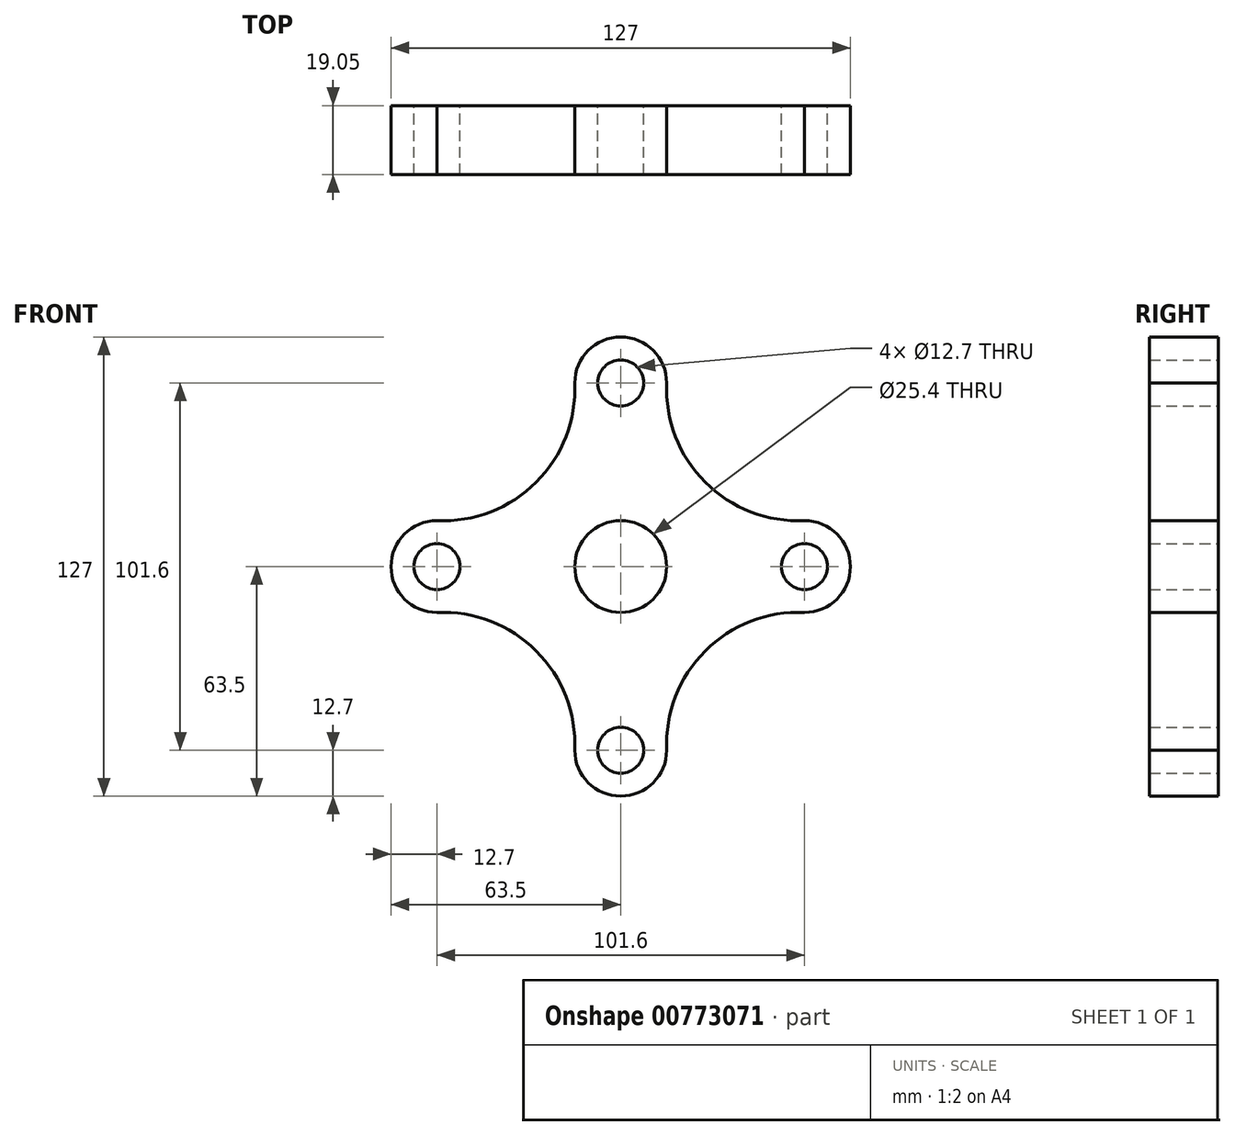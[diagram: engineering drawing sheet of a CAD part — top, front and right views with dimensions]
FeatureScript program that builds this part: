
annotation { "Feature Type Name" : "Feature", "Feature Type Description" : "" }
export const myFeature = defineFeature(function(context is Context, id is Id, definition is map)
    precondition{}
    {
        {
            var Q0;
            Q0=qCreatedBy(makeId("Front.planeOp"),FACE);
            var sketch = newSketch(context, id + "F0", { "sketchPlane" : qUnion([Q0])});
            skCircle(sketch, "E0", {"center": v(0, 50.8) * mm, "radius": 6.35 * mm});
            skArc(sketch, "E1", {"start": v(12.7, 50.8) * mm, "mid": v(0, 63.5) * mm, "end": v(-12.7, 50.8) * mm});
            skCircle(sketch, "E2.MirrorC", {"center": v(0, -50.8) * mm, "radius": 6.35 * mm});
            skArc(sketch, "E3.MirrorCS", {"start": v(12.7, -50.8) * mm, "mid": v(0, -63.5) * mm, "end": v(-12.7, -50.8) * mm});
            skCircle(sketch, "E4", {"center": v(-50.8, 0) * mm, "radius": 6.35 * mm});
            skArc(sketch, "E5", {"start": v(-50.8, 12.7) * mm, "mid": v(-63.5, 0) * mm, "end": v(-50.8, -12.7) * mm});
            skCircle(sketch, "E6.MirrorC", {"center": v(50.8, 0) * mm, "radius": 6.35 * mm});
            skArc(sketch, "E7.MirrorCS", {"start": v(50.8, 12.7) * mm, "mid": v(63.5, 0) * mm, "end": v(50.8, -12.7) * mm});
            skArc(sketch, "E8", {"start": v(-50.8, 12.7) * mm, "mid": v(-23.36, 23.36) * mm, "end": v(-12.7, 50.8) * mm});
            skArc(sketch, "E9", {"start": v(12.7, 50.8) * mm, "mid": v(23.36, 23.36) * mm, "end": v(50.8, 12.7) * mm});
            skArc(sketch, "E10", {"start": v(-12.7, -50.8) * mm, "mid": v(-23.36, -23.36) * mm, "end": v(-50.8, -12.7) * mm});
            skArc(sketch, "E11", {"start": v(50.8, -12.7) * mm, "mid": v(23.36, -23.36) * mm, "end": v(12.7, -50.8) * mm});
            skCircle(sketch, "E12", {"center": v(0, 0) * mm, "radius": 12.7 * mm});
            skSolve(sketch);
        }
        {
            var Q0;
            Q0=makeQuery(id+"F0.imprint","IMPRINT",FACE,{"disambiguationData":[TD([[makeQuery(id+"F0.imprint","IMPRINT",EDGE,{"derivedFrom":sQuery(id+"F0.wireOp",EDGE,"E0")}),-1.0]])]});
            extrude(context, id + "F1", {"entities" : qUnion([Q0]), "depth" : 19.05 * mm, "offsetDistance" : 25.4 * mm});
        }
    });
